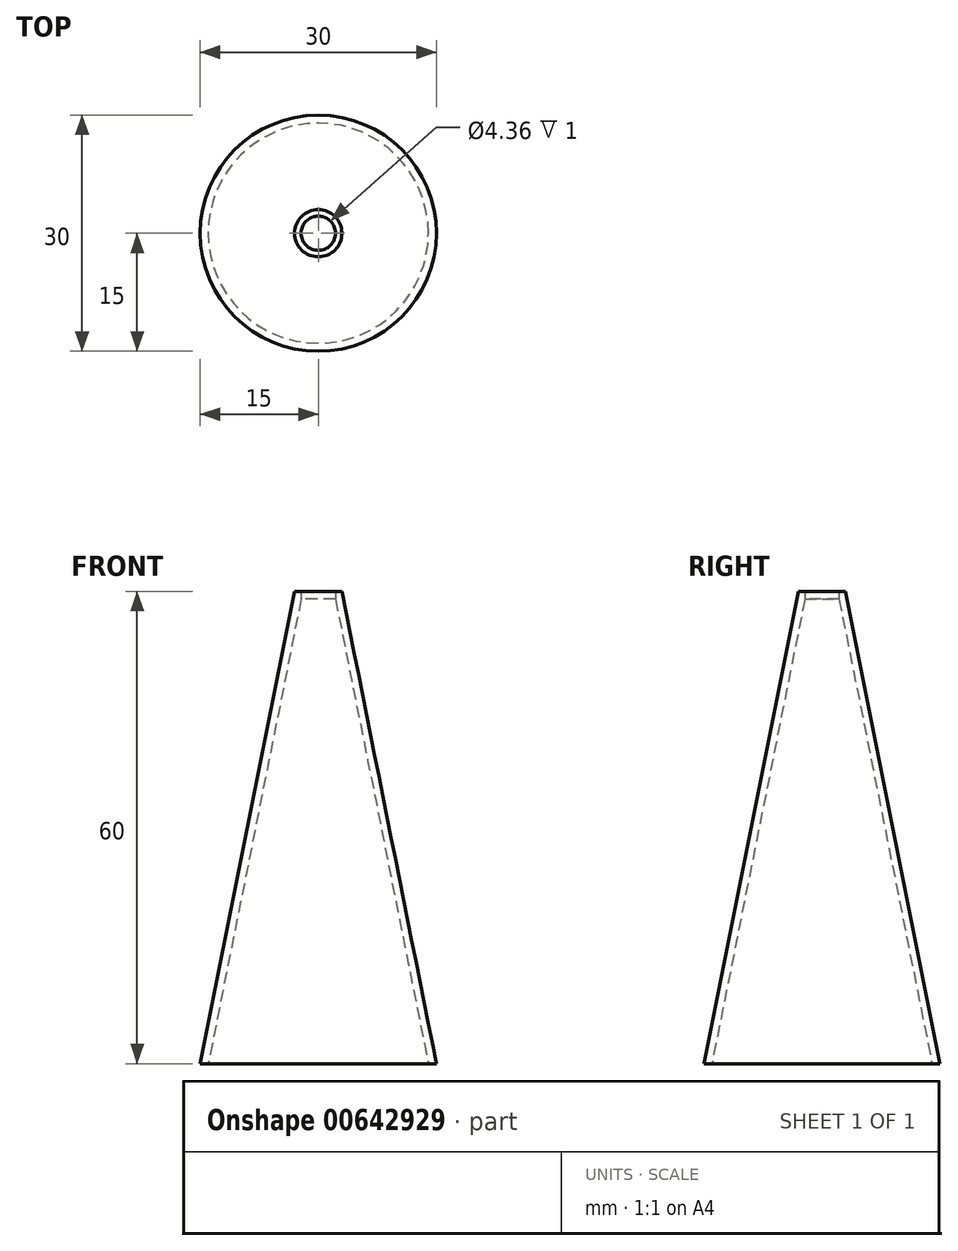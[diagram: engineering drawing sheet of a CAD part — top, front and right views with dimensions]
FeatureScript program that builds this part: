
annotation { "Feature Type Name" : "Feature", "Feature Type Description" : "" }
export const myFeature = defineFeature(function(context is Context, id is Id, definition is map)
    precondition{}
    {
        {
            var Q0;
            Q0=qCreatedBy(makeId("Top.planeOp"),FACE);
            cPlane(context, id + "F0", {"entities" : qUnion([Q0]), "cplaneType" : CPlaneType.OFFSET, "offset" : 60 * mm, "width" : 150 * mm, "height" : 150 * mm});
        }
        {
            var Q0;
            Q0=qCreatedBy(id+"F0.planeOp",FACE);
            var sketch = newSketch(context, id + "F1", { "sketchPlane" : qUnion([Q0])});
            skCircle(sketch, "E0", {"center": v(0, 0) * mm, "radius": 3 * mm});
            skSolve(sketch);
        }
        {
            var Q0;
            Q0=qCreatedBy(makeId("Top.planeOp"),FACE);
            var sketch = newSketch(context, id + "F2", { "sketchPlane" : qUnion([Q0])});
            skCircle(sketch, "E1", {"center": v(0, 0) * mm, "radius": 15 * mm});
            skSolve(sketch);
        }
        {
            var Q0;
            Q0=makeQuery(id+"F1.imprint","IMPRINT",FACE,{"disambiguationData":[TD([[makeQuery(id+"F1.imprint","IMPRINT",EDGE,{"derivedFrom":sQuery(id+"F1.wireOp",EDGE,"E0")}),1.0]])]});
            var Q1;
            Q1=makeQuery(id+"F2.imprint","IMPRINT",FACE,{"disambiguationData":[TD([[makeQuery(id+"F2.imprint","IMPRINT",EDGE,{"derivedFrom":sQuery(id+"F2.wireOp",EDGE,"E1")}),1.0]])]});
            loft(context, id + "F3", {"sheetProfilesArray" : [{ "sheetProfileEntities" : qUnion([Q0]) }, { "sheetProfileEntities" : qUnion([Q1]) }]});
        }
        {
            var Q0;
            Q0=makeQuery(id+"F3.opLoft","CAP_FACE",FACE,{"disambiguationData":[OSD([makeQuery(id+"F2.imprint","IMPRINT",FACE,{"disambiguationData":[TD([[makeQuery(id+"F2.imprint","IMPRINT",EDGE,{"derivedFrom":sQuery(id+"F2.wireOp",EDGE,"E1")}),1.0]])]})])],"isStart":true});
            var Q1;
            Q1=makeQuery(id+"F3.opLoft","SWEPT_BODY",BODY,{"disambiguationData":[OSD([makeQuery(id+"F1.imprint","IMPRINT",FACE,{"disambiguationData":[TD([[makeQuery(id+"F1.imprint","IMPRINT",EDGE,{"derivedFrom":sQuery(id+"F1.wireOp",EDGE,"E0")}),1.0]])]}),makeQuery(id+"F2.imprint","IMPRINT",FACE,{"disambiguationData":[TD([[makeQuery(id+"F2.imprint","IMPRINT",EDGE,{"derivedFrom":sQuery(id+"F2.wireOp",EDGE,"E1")}),1.0]])]})])]});
            shell(context, id + "F4", {"entities" : qUnion([Q0]), "parts" : qUnion([Q1]), "thickness" : 1 * mm});
        }
        {
            var Q0;
            Q0=makeQuery(id+"F4.opShell","OFFSET_FACE",FACE,{"disambiguationData":[OSD([makeQuery(id+"F1.imprint","IMPRINT",FACE,{"disambiguationData":[TD([[makeQuery(id+"F1.imprint","IMPRINT",EDGE,{"derivedFrom":sQuery(id+"F1.wireOp",EDGE,"E0")}),1.0]])]})])]});
            var sketch = newSketch(context, id + "F5", { "sketchPlane" : qUnion([Q0])});
            skCircle(sketch, "E2.0", {"center": v(0, 0) * mm, "radius": 2.18 * mm});
            skSolve(sketch);
        }
        {
            var Q0;
            Q0=makeQuery(id+"F5.imprint","IMPRINT",FACE,{"disambiguationData":[TD([[makeQuery(id+"F5.imprint","IMPRINT",EDGE,{"derivedFrom":sQuery(id+"F5.wireOp",EDGE,"E2.0")}),1.0]])]});
            extrude(context, id + "F6", {"entities" : qUnion([Q0]), "operationType" : NewBodyOperationType.REMOVE, "oppositeDirection" : true, "depth" : 25 * mm, "offsetDistance" : 25 * mm});
        }
    });
